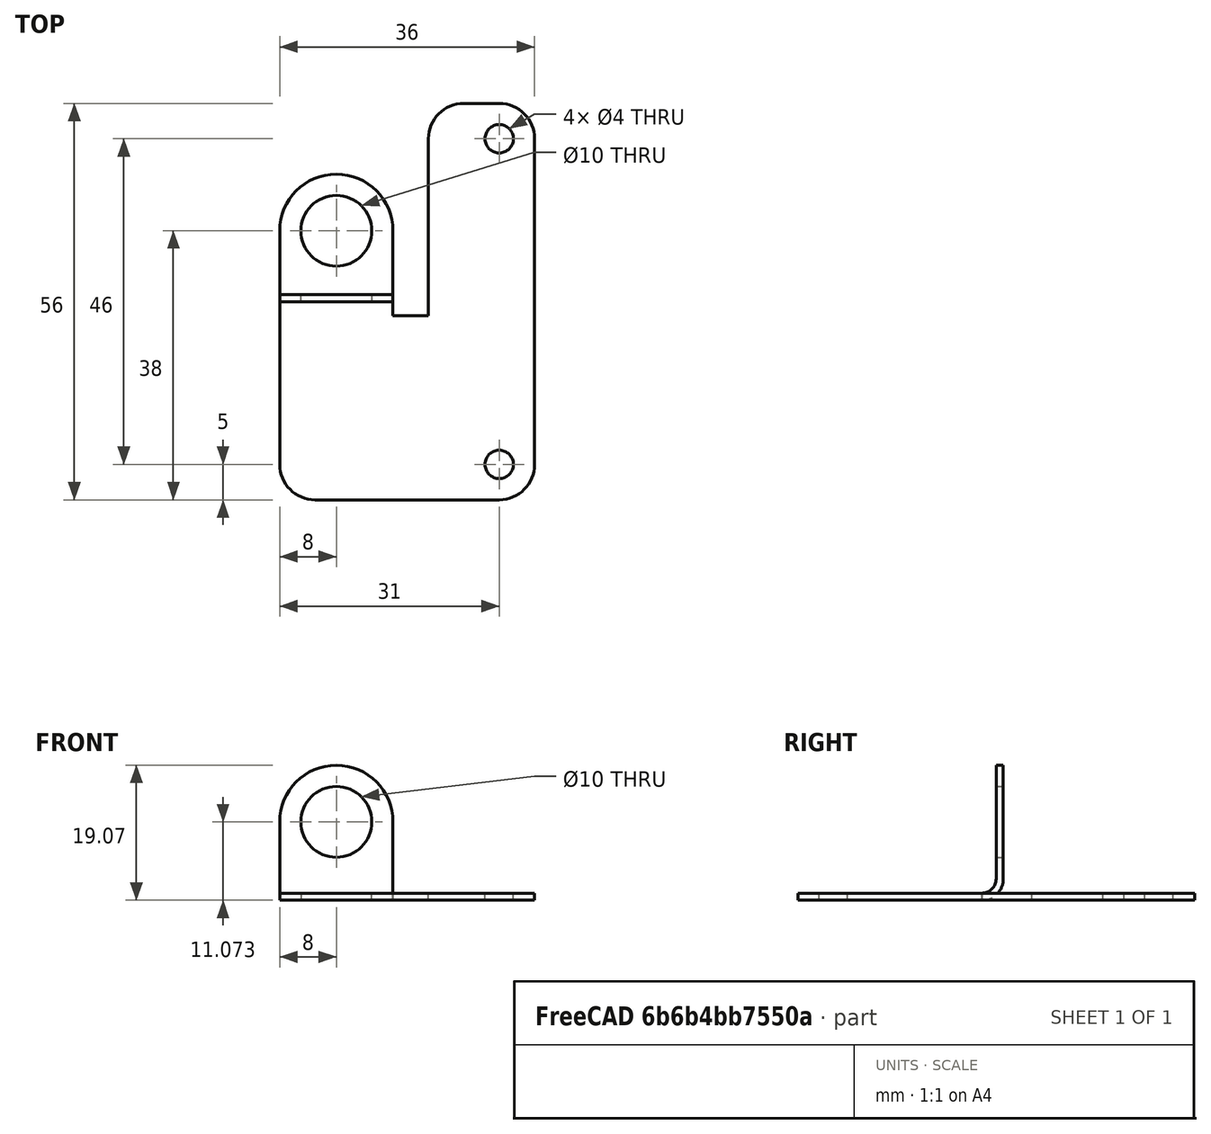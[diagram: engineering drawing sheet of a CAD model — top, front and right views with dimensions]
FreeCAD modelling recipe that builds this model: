
FCSTD DOCUMENT  (FreeCAD 0.21R32532 (Git))
Label: sensor_holder
License: All rights reserved
LicenseURL: http://en.wikipedia.org/wiki/All_rights_reserved
objects: Sketcher::SketchObject×7, TechDraw::DrawViewDimension×5, TechDraw::DrawViewPart×3, PartDesign::SubShapeBinder×1, PartDesign::Pad×1, PartDesign::Hole×1, PartDesign::FeaturePython×1, PartDesign::Body×1, TechDraw::DrawSVGTemplate×1, TechDraw::DrawPage×1, Part::Feature×1
note: 23 computed .brp shape members not serialized (recipe doc carries the construction recipe); baked Part::Feature solids carry a one-line shape summary decoded from their .brp

FEATURE [Sketcher::SketchObject] Sketch
  FullyConstrained = true
  MapMode = 5
  sketch-geometry (2):
    g0: Circle CenterX=0 CenterY=23 CenterZ=0 NormalX=0 NormalY=0 NormalZ=1 AngleXU=0 Radius=2
    g1: Circle CenterX=0 CenterY=-23 CenterZ=0 NormalX=0 NormalY=0 NormalZ=1 AngleXU=0 Radius=2
  constraints (5):
    c: PointOnObject(g0,g-2)
    c: Equal(g1,g0)
    c: Diameter(g1) = 4
    c: Symmetric(g1,g0,g-1)
    c: DistanceY(g1,g0) = 46
FEATURE [PartDesign::SubShapeBinder] Binder
  BindCopyOnChange = 0
  BindMode = 0
  ClaimChildren = false
  Context = -> Body [Binder.]
  Fuse = false
  MakeFace = false
  OffsetFill = false
  OffsetIntersection = false
  OffsetJoinType = 0
  OffsetOpenResult = false
  PartialLoad = false
  Relative = true
  Support = -> [Sketch]
  _Version = 2
FEATURE [Sketcher::SketchObject] Sketch001
  ExternalGeometry = -> [Binder]
  FullyConstrained = true
  MapMode = 5
  Support = -> [XY_Plane]
  sketch-geometry (13):
    g0: ArcOfCircle CenterX=6.8319e-12 CenterY=-23 CenterZ=0 NormalX=0 NormalY=0 NormalZ=1 AngleXU=0 Radius=5 StartAngle=4.71239 EndAngle=6.28319
    g1: LineSegment StartX=5 StartY=-23 StartZ=0 EndX=5 EndY=23 EndZ=0
    g2: LineSegment StartX=-10 StartY=23 StartZ=0 EndX=-10 EndY=-2 EndZ=0
    g3: LineSegment StartX=-10 StartY=-2 StartZ=0 EndX=-15 EndY=-2 EndZ=0
    g4: LineSegment StartX=-26 StartY=-28 StartZ=0 EndX=7.2333e-12 EndY=-28 EndZ=0
    g5: ArcOfCircle CenterX=-26 CenterY=-23 CenterZ=0 NormalX=0 NormalY=0 NormalZ=1 AngleXU=0 Radius=5 StartAngle=3.14159 EndAngle=4.71239
    g6: ArcOfCircle CenterX=-23 CenterY=10 CenterZ=0 NormalX=0 NormalY=0 NormalZ=1 AngleXU=0 Radius=8 StartAngle=8.949e-13 EndAngle=3.14159
    g7: LineSegment StartX=-31 StartY=-23 StartZ=0 EndX=-31 EndY=10 EndZ=0
    g8: LineSegment StartX=-15 StartY=-2 StartZ=0 EndX=-15 EndY=10 EndZ=0
    g9: Circle CenterX=-23 CenterY=10 CenterZ=0 NormalX=0 NormalY=0 NormalZ=1 AngleXU=0 Radius=5
    g10: ArcOfCircle CenterX=-1.48111e-11 CenterY=23 CenterZ=0 NormalX=0 NormalY=0 NormalZ=1 AngleXU=0 Radius=5 StartAngle=7.3e-15 EndAngle=1.5708
    g11: ArcOfCircle CenterX=-5 CenterY=23 CenterZ=0 NormalX=0 NormalY=0 NormalZ=1 AngleXU=0 Radius=5 StartAngle=1.5708 EndAngle=3.14159
    g12: LineSegment StartX=-5 StartY=28 StartZ=0 EndX=-2.15717e-10 EndY=28 EndZ=0
  constraints (33):
    c: Coincident(g10,g-3)
    c: Coincident(g0,g-4)
    c: Vertical(g1)
    c: Tangent(g1,g10) = -1.5708
    c: Tangent(g1,g0) = -1.5708
    c: Vertical(g2)
    c: Coincident(g3,g2)
    c: Horizontal(g4)
    c: Tangent(g4,g5) = -1.5708
    c: Horizontal(g3)
    c: Diameter(g0) = 10
    c: Equal(g0,g5)
    c: Vertical(g7)
    c: Coincident(g8,g3)
    c: Vertical(g8)
    c: DistanceX(g3,g3) = 5
    c: Coincident(g9,g6)
    c: Diameter(g9) = 10
    c: Diameter(g6) = 16
    c: Tangent(g8,g6) = -1.5708
    c: Tangent(g7,g6) = 1.5708
    c: DistanceY(g3,g6) = 12
    c: Tangent(g5,g7) = 1.5708
    c: Tangent(g0,g4) = -1.5708
    c: DistanceX(g3) = -15  'bend_x'
    c: DistanceY(g3) = -2  'bend_y'
    c: Horizontal(g12)
    c: Tangent(g11,g2) = -1.5708
    c: Equal(g10,g11)
    c: DistanceX(g12,g12) = 5
    c: Tangent(g12,g11) = 1.5708
    c: Tangent(g12,g10) = 1.5708
    c: DistanceY(g2,g11) = 30
FEATURE [PartDesign::Pad] Pad
  Direction = (0,0,1)
  Length = 1
  Length2 = 10
  Profile = -> Sketch001
  ReferenceAxis = -> Sketch001 [N_Axis]
  Type = 0
FEATURE [PartDesign::Hole] Hole
  BaseFeature = -> Pad
  CustomThreadClearance = 0
  Depth = 25
  DepthType = 0
  Diameter = 4
  DrillForDepth = false
  DrillPoint = 1
  DrillPointAngle = 118
  HoleCutCountersinkAngle = 90
  HoleCutCustomValues = false
  HoleCutDepth = 0
  HoleCutDiameter = 6.1
  HoleCutType = 0
  ModelThread = false
  Profile = -> Binder
  Reversed = true
  Tapered = false
  TaperedAngle = 90
  ThreadClass = 0
  ThreadDepth = 25
  ThreadDepthType = 0
  ThreadDirection = 0
  ThreadFit = 0
  ThreadSize = 0
  ThreadType = 0
  Threaded = false
  UseCustomThreadClearance = false
FEATURE [Sketcher::SketchObject] Sketch002
  AttachmentOffset = pos=(0,0,1) rot=(0,0,1;0rad)
  FullyConstrained = true
  MapMode = 5
  Placement = pos=(0,0,1) rot=(0,0,1;0rad)
  Support = -> [XY_Plane]
  expr: .AttachmentOffset.Base.z = Pad.Length
  expr: Constraints[1] = Sketch001.Constraints.bend_x
  expr: Constraints[2] = Sketch001.Constraints.bend_y
  sketch-geometry (1):
    g0: LineSegment StartX=-15 StartY=-2 StartZ=0 EndX=-115 EndY=-2 EndZ=0
  constraints (4):
    c: Horizontal(g0)
    c: DistanceX(g0) = -15
    c: DistanceY(g0) = -2
    c: DistanceX(g0,g0) = 100
FEATURE [PartDesign::FeaturePython] Fold  # WARN: FeaturePython — macro-defined, semantics opaque (R4)
  BaseFeature = -> Hole
  BendLine = -> Sketch002
  Position = 0
  angle = 90
  baseObject = -> Hole [Face5]
  invert = false
  invertbend = false
  kfactor = 0.5
  radius = 2
  unfold = false
FEATURE [PartDesign::Body] Body  label="Body_material_0.50ansi"
  Group = -> [Sketch001,Binder,Pad,Hole,Sketch002,Fold]
  Origin = -> Origin
  Tip = -> Fold
FEATURE [TechDraw::DrawSVGTemplate] Template
  Height = 210
  Orientation = 1
  Template = <path>
  Width = 297
FEATURE [TechDraw::DrawViewPart] View
  CoarseView = false
  Direction = (0,0,1)
  Focus = 100
  HardHidden = false
  IsoCount = 0
  IsoHidden = false
  IsoVisible = false
  LockPosition = false
  Perspective = false
  Rotation = 0
  ScaleType = 0
  SeamHidden = false
  SeamVisible = true
  SmoothHidden = false
  SmoothVisible = true
  Source = -> [Body]
  X = 86.5
  XDirection = (1,0,0)
  Y = 105
  expr: Y = Template.Height / 2
FEATURE [TechDraw::DrawViewPart] View001
  CoarseView = false
  Direction = (1,0,0)
  Focus = 100
  HardHidden = false
  IsoCount = 0
  IsoHidden = false
  IsoVisible = false
  LockPosition = false
  Perspective = false
  Rotation = 0
  ScaleType = 0
  SeamHidden = false
  SeamVisible = true
  SmoothHidden = false
  SmoothVisible = true
  Source = -> [Body]
  X = 217.5
  XDirection = (0,1,-1.19209e-07)
  Y = 105
  expr: Y = Template.Height / 2
FEATURE [TechDraw::DrawViewPart] View002
  CoarseView = false
  Direction = (0,-1,0)
  Focus = 100
  HardHidden = false
  IsoCount = 0
  IsoHidden = false
  IsoVisible = false
  LockPosition = false
  Perspective = false
  Rotation = 0
  ScaleType = 0
  SeamHidden = false
  SeamVisible = true
  SmoothHidden = false
  SmoothVisible = true
  Source = -> [Body]
  X = 148.5
  XDirection = (1,0,0)
  Y = 105
  expr: Y = Template.Height / 2
FEATURE [TechDraw::DrawViewDimension] Dimension001
  AngleOverride = false
  Arbitrary = false
  ArbitraryTolerances = false
  EqualTolerance = true
  ExtensionAngle = 0
  FormatSpec = %.2w
  FormatSpecOverTolerance = %+.2w
  FormatSpecUnderTolerance = %+.2w
  Inverted = false
  LineAngle = 0
  LockPosition = false
  MeasureType = 1
  OverTolerance = 0
  References2D = -> [View]
  Rotation = 0
  ScaleType = 0
  TheoreticalExact = false
  Type = 2
  UnderTolerance = 0
  X = 30.1969
  Y = 4.20419
FEATURE [TechDraw::DrawViewDimension] Dimension002
  AngleOverride = false
  Arbitrary = false
  ArbitraryTolerances = false
  EqualTolerance = true
  ExtensionAngle = 0
  FormatSpec = %.2w
  FormatSpecOverTolerance = %+.2w
  FormatSpecUnderTolerance = %+.2w
  Inverted = false
  LineAngle = 0
  LockPosition = false
  MeasureType = 1
  OverTolerance = 0
  References2D = -> [View]
  Rotation = 0
  ScaleType = 0
  TheoreticalExact = false
  Type = 1
  UnderTolerance = 0
  X = 0.309853
  Y = -39.2461
FEATURE [TechDraw::DrawViewDimension] Dimension003
  AngleOverride = false
  Arbitrary = false
  ArbitraryTolerances = false
  EqualTolerance = true
  ExtensionAngle = 0
  FormatSpec = %.2w
  FormatSpecOverTolerance = %+.2w
  FormatSpecUnderTolerance = %+.2w
  Inverted = false
  LineAngle = 0
  LockPosition = false
  MeasureType = 1
  OverTolerance = 0
  References2D = -> [View002]
  Rotation = 0
  ScaleType = 0
  TheoreticalExact = false
  Type = 2
  UnderTolerance = 0
  X = 25.1812
  Y = -2.14553
FEATURE [TechDraw::DrawViewDimension] Dimension004
  AngleOverride = false
  Arbitrary = false
  ArbitraryTolerances = false
  EqualTolerance = true
  ExtensionAngle = 0
  FormatSpec = R%.2w
  FormatSpecOverTolerance = %+.2w
  FormatSpecUnderTolerance = %+.2w
  Inverted = false
  LineAngle = 0
  LockPosition = false
  MeasureType = 1
  OverTolerance = 0
  References2D = -> [View001]
  Rotation = 0
  ScaleType = 0
  TheoreticalExact = false
  Type = 4
  UnderTolerance = 0
  X = -2.33735
  Y = 6.64929
FEATURE [TechDraw::DrawViewDimension] Dimension
  AngleOverride = false
  Arbitrary = false
  ArbitraryTolerances = false
  EqualTolerance = true
  ExtensionAngle = 0
  FormatSpec = %.2w
  FormatSpecOverTolerance = %+.2w
  FormatSpecUnderTolerance = %+.2w
  Inverted = false
  LineAngle = 0
  LockPosition = false
  MeasureType = 1
  OverTolerance = 0
  References2D = -> [View]
  Rotation = 0
  ScaleType = 0
  TheoreticalExact = false
  Type = 1
  UnderTolerance = 0
  X = -8.63314
  Y = 16.5828
FEATURE [TechDraw::DrawPage] Page
  KeepUpdated = true
  NextBalloonIndex = 1
  ProjectionType = 0
  Template = -> Template
  Views = -> [View,View001,View002,Dimension001,Dimension002,Dimension003,Dimension004,Dimension]
FEATURE [Part::Feature] Unfold
  shape: bbox 36 x 56 x 1 mm, 17 faces (baked)
FEATURE [Sketcher::SketchObject] Unfold_Sketch
  FullyConstrained = false
  sketch-geometry (18):
    g0: ArcOfCircle CenterX=-23 CenterY=10 CenterZ=0 NormalX=0 NormalY=0 NormalZ=1 AngleXU=0 Radius=8 StartAngle=8.949e-13 EndAngle=3.14159
    g1: LineSegment StartX=-10 StartY=-2 StartZ=0 EndX=-15 EndY=-2 EndZ=0
    g2: LineSegment StartX=-10 StartY=23 StartZ=0 EndX=-10 EndY=-2 EndZ=0
    g3: ArcOfCircle CenterX=-5 CenterY=23 CenterZ=0 NormalX=0 NormalY=0 NormalZ=1 AngleXU=0 Radius=5 StartAngle=1.5708 EndAngle=3.14159
    g4: LineSegment StartX=-5 StartY=28 StartZ=0 EndX=-2.15717e-10 EndY=28 EndZ=0
    g5: ArcOfCircle CenterX=-1.48111e-11 CenterY=23 CenterZ=0 NormalX=0 NormalY=0 NormalZ=1 AngleXU=0 Radius=5 StartAngle=7.3e-15 EndAngle=1.5708
    g6: LineSegment StartX=5 StartY=-23 StartZ=0 EndX=5 EndY=23 EndZ=0
    g7: ArcOfCircle CenterX=6.8319e-12 CenterY=-23 CenterZ=0 NormalX=0 NormalY=0 NormalZ=1 AngleXU=0 Radius=5 StartAngle=4.71239 EndAngle=6.28319
    g8: LineSegment StartX=-26 StartY=-28 StartZ=0 EndX=7.2333e-12 EndY=-28 EndZ=0
    g9: ArcOfCircle CenterX=-26 CenterY=-23 CenterZ=0 NormalX=0 NormalY=0 NormalZ=1 AngleXU=0 Radius=5 StartAngle=3.14159 EndAngle=4.71239
    g10: Circle CenterX=-23 CenterY=10 CenterZ=0 NormalX=0 NormalY=0 NormalZ=1 AngleXU=0 Radius=5
    g11: Circle CenterX=0 CenterY=-23 CenterZ=0 NormalX=0 NormalY=0 NormalZ=1 AngleXU=-3.14159 Radius=2
    g12: Circle CenterX=0 CenterY=23 CenterZ=0 NormalX=0 NormalY=0 NormalZ=1 AngleXU=-3.14159 Radius=2
    g13: LineSegment StartX=-31 StartY=-23 StartZ=0 EndX=-31 EndY=-2 EndZ=0
    g14: LineSegment StartX=-31 StartY=-2 StartZ=0 EndX=-31 EndY=1.92699 EndZ=0
    g15: LineSegment StartX=-31 StartY=1.92699 StartZ=0 EndX=-31 EndY=10 EndZ=0
    g16: LineSegment StartX=-15 StartY=1.92699 StartZ=0 EndX=-15 EndY=-2 EndZ=0
    g17: LineSegment StartX=-15 StartY=1.92699 StartZ=0 EndX=-15 EndY=10 EndZ=0
FEATURE [Sketcher::SketchObject] Unfold_Sketch_Outline
  FullyConstrained = false
  sketch-geometry (15):
    g0: LineSegment StartX=-15 StartY=1.92699 StartZ=0 EndX=-15 EndY=10 EndZ=0
    g1: ArcOfCircle CenterX=-23 CenterY=10 CenterZ=0 NormalX=0 NormalY=0 NormalZ=1 AngleXU=0 Radius=8 StartAngle=8.949e-13 EndAngle=3.14159
    g2: LineSegment StartX=-31 StartY=1.92699 StartZ=0 EndX=-31 EndY=10 EndZ=0
    g3: LineSegment StartX=-31 StartY=-2 StartZ=0 EndX=-31 EndY=1.92699 EndZ=0
    g4: LineSegment StartX=-31 StartY=-23 StartZ=0 EndX=-31 EndY=-2 EndZ=0
    g5: ArcOfCircle CenterX=-26 CenterY=-23 CenterZ=0 NormalX=0 NormalY=0 NormalZ=1 AngleXU=0 Radius=5 StartAngle=3.14159 EndAngle=4.71239
    g6: LineSegment StartX=-26 StartY=-28 StartZ=0 EndX=7.2333e-12 EndY=-28 EndZ=0
    g7: ArcOfCircle CenterX=6.8319e-12 CenterY=-23 CenterZ=0 NormalX=0 NormalY=0 NormalZ=1 AngleXU=0 Radius=5 StartAngle=4.71239 EndAngle=6.28319
    g8: LineSegment StartX=5 StartY=-23 StartZ=0 EndX=5 EndY=23 EndZ=0
    g9: ArcOfCircle CenterX=-1.48111e-11 CenterY=23 CenterZ=0 NormalX=0 NormalY=0 NormalZ=1 AngleXU=0 Radius=5 StartAngle=7.3e-15 EndAngle=1.5708
    g10: LineSegment StartX=-5 StartY=28 StartZ=0 EndX=-2.15717e-10 EndY=28 EndZ=0
    g11: ArcOfCircle CenterX=-5 CenterY=23 CenterZ=0 NormalX=0 NormalY=0 NormalZ=1 AngleXU=0 Radius=5 StartAngle=1.5708 EndAngle=3.14159
    g12: LineSegment StartX=-10 StartY=23 StartZ=0 EndX=-10 EndY=-2 EndZ=0
    g13: LineSegment StartX=-10 StartY=-2 StartZ=0 EndX=-15 EndY=-2 EndZ=0
    g14: LineSegment StartX=-15 StartY=1.92699 StartZ=0 EndX=-15 EndY=-2 EndZ=0
FEATURE [Sketcher::SketchObject] Unfold_Sketch_Internal
  FullyConstrained = false
  sketch-geometry (3):
    g0: Circle CenterX=-23 CenterY=10 CenterZ=0 NormalX=0 NormalY=0 NormalZ=1 AngleXU=0 Radius=5
    g1: Circle CenterX=0 CenterY=23 CenterZ=0 NormalX=0 NormalY=0 NormalZ=1 AngleXU=-3.14159 Radius=2
    g2: Circle CenterX=0 CenterY=-23 CenterZ=0 NormalX=0 NormalY=0 NormalZ=1 AngleXU=-3.14159 Radius=2
FEATURE [Sketcher::SketchObject] Unfold_Sketch_bends
  FullyConstrained = false
  Placement = pos=(0,-0.00391043,0.0112897) rot=(1,0,0;0.333439rad)
  sketch-geometry (1):
    g0: LineSegment StartX=-31 StartY=-0.034494 StartZ=0 EndX=-15 EndY=-0.034494 EndZ=0
note: 1 file-system path scrubbed to <path> (originals preserved in the JSON sidecar)
